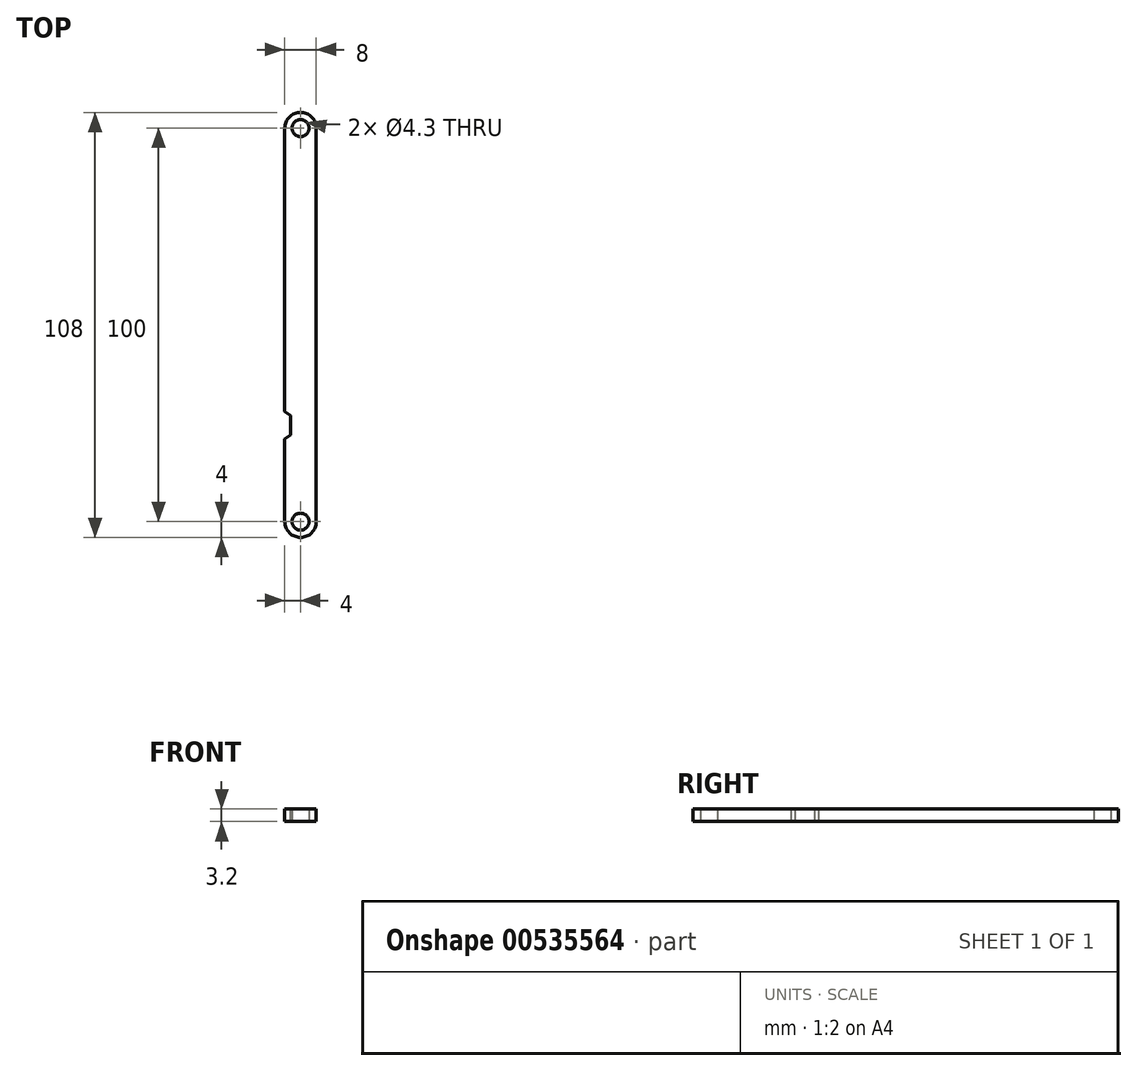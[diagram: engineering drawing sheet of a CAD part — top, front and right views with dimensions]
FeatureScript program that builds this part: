
annotation { "Feature Type Name" : "Feature", "Feature Type Description" : "" }
export const myFeature = defineFeature(function(context is Context, id is Id, definition is map)
    precondition{}
    {
        {
            var Q0;
            Q0=qCreatedBy(makeId("Top.planeOp"),FACE);
            var sketch = newSketch(context, id + "F0", { "sketchPlane" : qUnion([Q0])});
            skLineSegment(sketch, "E0", {"start": v(0, 50) * mm, "end": v(0, -50) * mm});
            skCircle(sketch, "E1", {"center": v(-4, 50) * mm, "radius": 4 * mm});
            skCircle(sketch, "E2", {"center": v(-4, -50) * mm, "radius": 4 * mm});
            skLineSegment(sketch, "E3", {"start": v(-8, 50) * mm, "end": v(-8, -50) * mm});
            skCircle(sketch, "E4", {"center": v(-4, 50) * mm, "radius": 2.15 * mm});
            skCircle(sketch, "E5", {"center": v(-4, -50) * mm, "radius": 2.15 * mm});
            skSolve(sketch);
        }
        {
            var Q0;
            Q0 = qSketchRegion(id + "F0", true);
            extrude(context, id + "F1", {"entities" : qUnion([Q0]), "depth" : 3.2 * mm, "offsetDistance" : 25 * mm});
        }
        {
            var Q0;
            Q0=qCreatedBy(makeId("Top.planeOp"),FACE);
            var sketch = newSketch(context, id + "F2", { "sketchPlane" : qUnion([Q0])});
            skLineSegment(sketch, "E6", {"start": v(-8, -22) * mm, "end": v(-8, -29) * mm});
            skLineSegment(sketch, "E7", {"start": v(-8, -29) * mm, "end": v(-6.5, -28) * mm});
            skLineSegment(sketch, "E8", {"start": v(-6.5, -28) * mm, "end": v(-6.5, -23) * mm});
            skLineSegment(sketch, "E9", {"start": v(-6.5, -23) * mm, "end": v(-8, -22) * mm});
            skSolve(sketch);
        }
        {
            var Q0;
            Q0 = qSketchRegion(id + "F2", true);
            extrude(context, id + "F3", {"entities" : qUnion([Q0]), "operationType" : NewBodyOperationType.REMOVE, "oppositeDirection" : true, "depth" : 25 * mm, "offsetDistance" : 25 * mm, "symmetric" : true});
        }
    });
